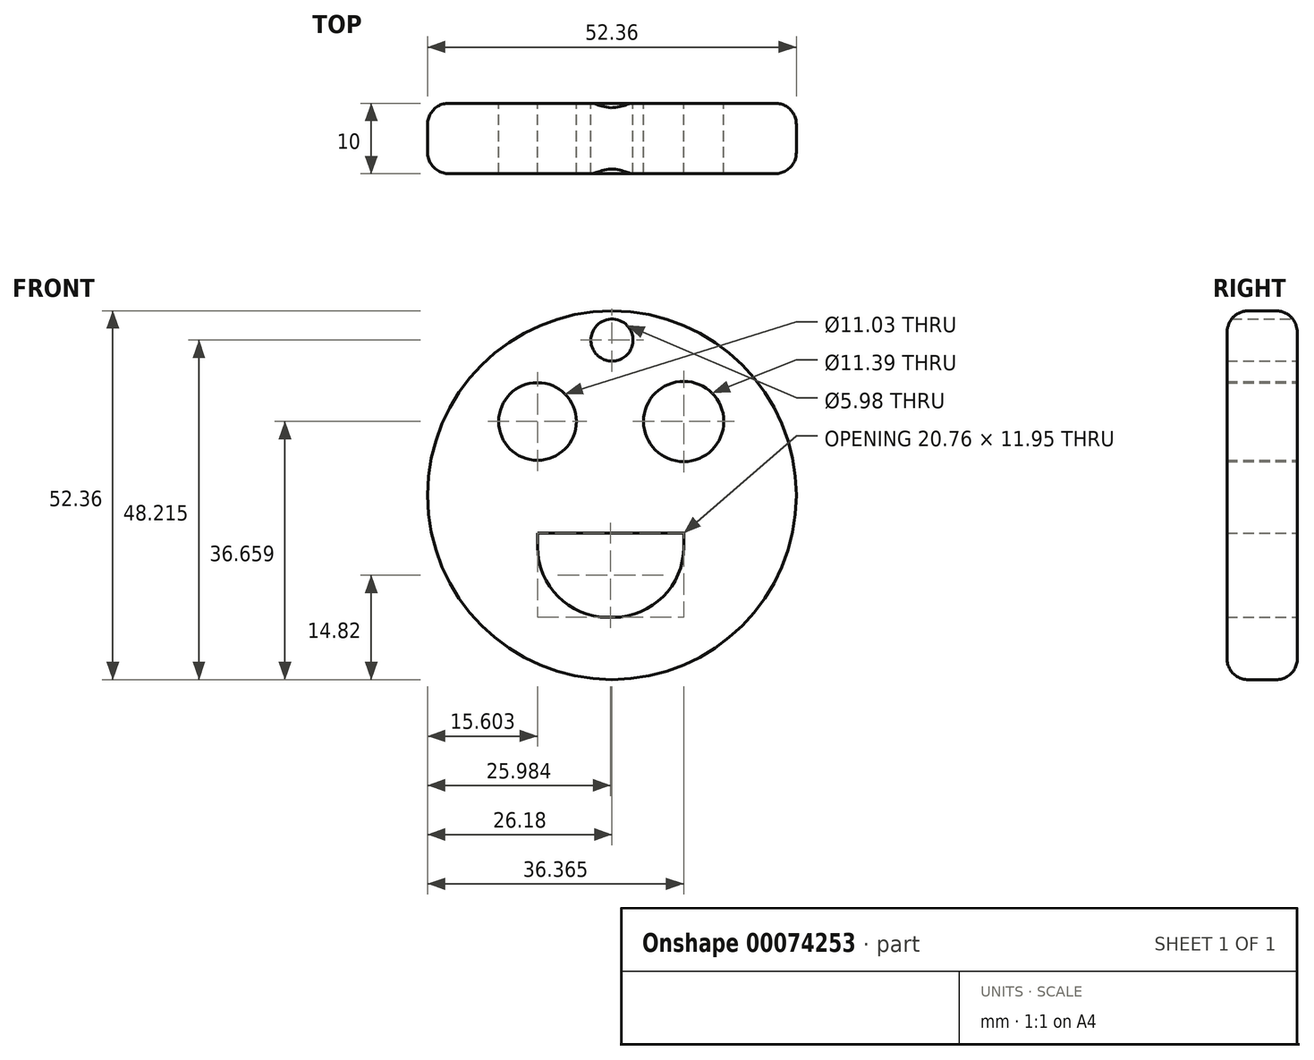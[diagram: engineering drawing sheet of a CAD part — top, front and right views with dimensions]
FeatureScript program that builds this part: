
annotation { "Feature Type Name" : "Feature", "Feature Type Description" : "" }
export const myFeature = defineFeature(function(context is Context, id is Id, definition is map)
    precondition{}
    {
        {
            var Q0;
            Q0=qCreatedBy(makeId("Front.planeOp"),FACE);
            var sketch = newSketch(context, id + "F0", { "sketchPlane" : qUnion([Q0])});
            skCircle(sketch, "E0", {"center": v(0, 0) * mm, "radius": 26.18 * mm});
            skCircle(sketch, "E1", {"center": v(-10.58, 10.48) * mm, "radius": 5.52 * mm});
            skCircle(sketch, "E2", {"center": v(10.18, 10.48) * mm, "radius": 5.7 * mm});
            skLineSegment(sketch, "E3.bottom", {"start": v(-10.58, -5.39) * mm, "end": v(10.18, -5.39) * mm});
            skLineSegment(sketch, "E3.top", {"start": v(-0.58, -17.33) * mm, "end": v(0.18, -17.33) * mm});
            skLineSegment(sketch, "E3.left", {"start": v(-10.58, -5.39) * mm, "end": v(-10.58, -7.33) * mm});
            skLineSegment(sketch, "E3.right", {"start": v(10.18, -5.39) * mm, "end": v(10.18, -7.33) * mm});
            skPoint(sketch, "E4.visualSharp", {"position": v(-10.58, -17.33) * mm});
            skArc(sketch, "E4.filletArc", {"start": v(-10.58, -7.33) * mm, "mid": v(-7.65, -14.4) * mm, "end": v(-0.58, -17.33) * mm});
            skPoint(sketch, "E5.visualSharp", {"position": v(10.18, -17.33) * mm});
            skArc(sketch, "E5.filletArc", {"start": v(0.18, -17.33) * mm, "mid": v(7.26, -14.4) * mm, "end": v(10.18, -7.33) * mm});
            skCircle(sketch, "E6", {"center": v(0, 22.03) * mm, "radius": 2.99 * mm});
            skSolve(sketch);
        }
        {
            var Q0;
            Q0=makeQuery(id+"F0.imprint","IMPRINT",FACE,{"disambiguationData":[TD([[makeQuery(id+"F0.imprint","IMPRINT",EDGE,{"derivedFrom":sQuery(id+"F0.wireOp",EDGE,"E0")}),1.0]])]});
            extrude(context, id + "F1", {"entities" : qUnion([Q0]), "depth" : 10 * mm});
        }
        {
            var Q0;
            Q0=makeQuery(id+"F1.opExtrude","CAP_EDGE",EDGE,{"disambiguationData":[OSD([sQuery(id+"F0.wireOp",EDGE,"E0")])],"isStart":false});
            var Q1;
            Q1=makeQuery(id+"F1.opExtrude","CAP_EDGE",EDGE,{"disambiguationData":[OSD([sQuery(id+"F0.wireOp",EDGE,"E0")])],"isStart":true});
            fillet(context, id + "F2", {"entities" : qUnion([Q0, Q1]), "radius" : 3 * mm, "tangentPropagation" : true, "allowEdgeOverflow" : false});
        }
    });
